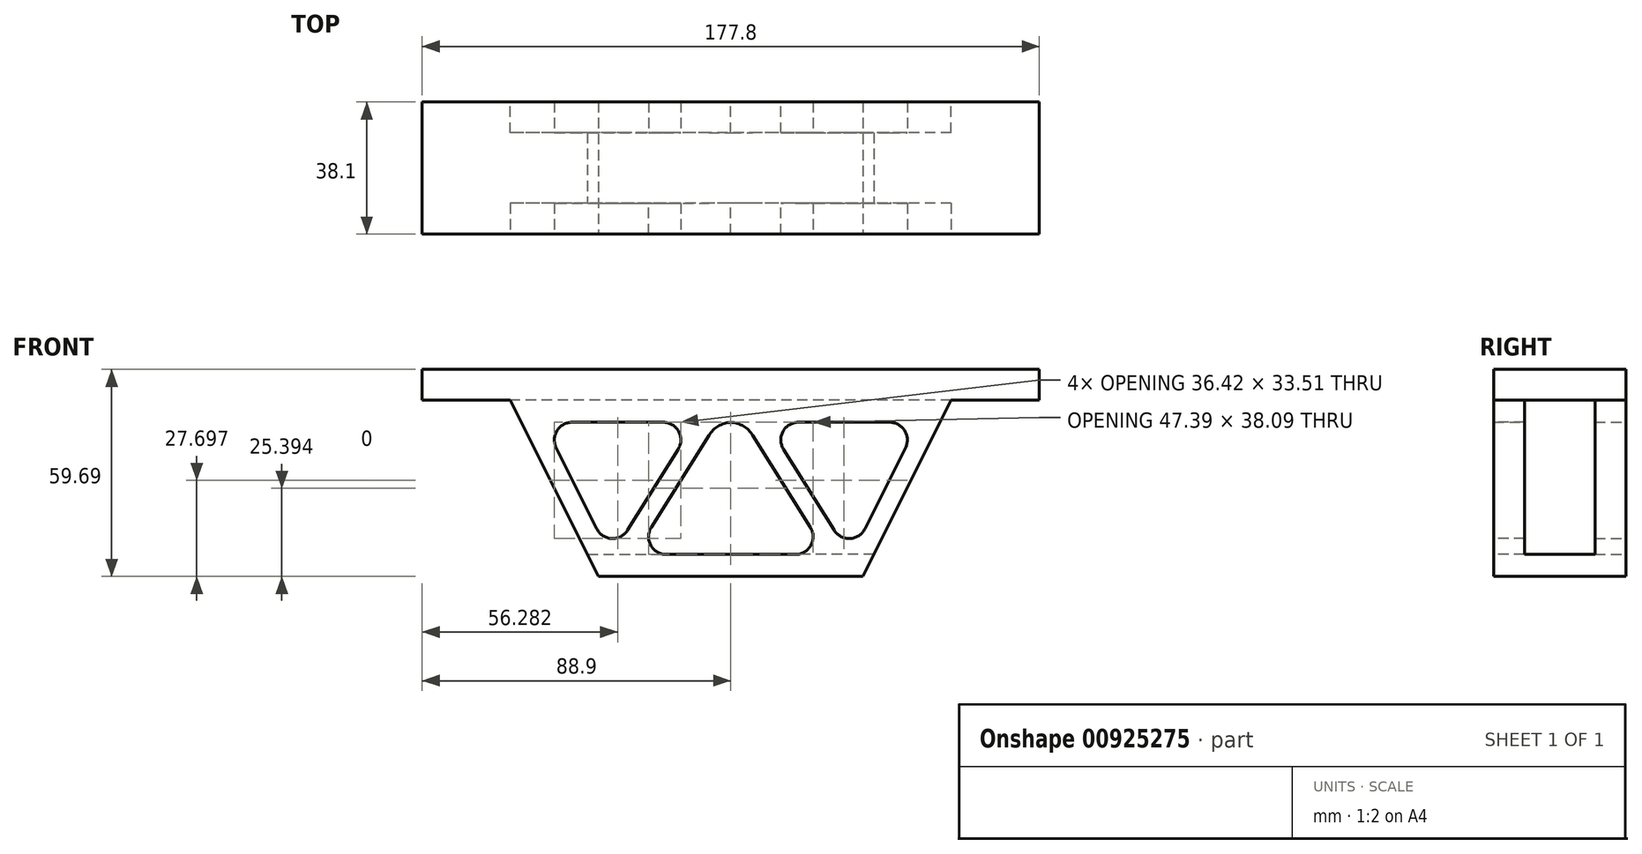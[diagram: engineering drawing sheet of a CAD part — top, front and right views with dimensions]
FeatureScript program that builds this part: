
annotation { "Feature Type Name" : "Feature", "Feature Type Description" : "" }
export const myFeature = defineFeature(function(context is Context, id is Id, definition is map)
    precondition{}
    {
        {
            var Q0;
            Q0=qCreatedBy(makeId("Right.planeOp"),FACE);
            var sketch = newSketch(context, id + "F0", { "sketchPlane" : qUnion([Q0])});
            skLineSegment(sketch, "E0.bottom", {"start": v(0, 0) * mm, "end": v(38.1, 0) * mm});
            skLineSegment(sketch, "E0.top", {"start": v(0, 8.9) * mm, "end": v(38.1, 8.9) * mm});
            skLineSegment(sketch, "E0.left", {"start": v(0, 0) * mm, "end": v(0, 8.9) * mm});
            skLineSegment(sketch, "E0.right", {"start": v(38.1, 0) * mm, "end": v(38.1, 8.9) * mm});
            skSolve(sketch);
        }
        {
            var Q0;
            Q0=makeQuery(id+"F0.imprint","IMPRINT",FACE,{"disambiguationData":[TD([[makeQuery(id+"F0.imprint","IMPRINT",EDGE,{"derivedFrom":sQuery(id+"F0.wireOp",EDGE,"E0.bottom")}),1.0]])]});
            extrude(context, id + "F1", {"entities" : qUnion([Q0]), "depth" : 177.8 * mm, "offsetDistance" : 25.4 * mm});
        }
        {
            var Q0;
            Q0=makeQuery(id+"F1.opExtrude","SWEPT_FACE",FACE,{"disambiguationData":[OSD([sQuery(id+"F0.wireOp",EDGE,"E0.left")])]});
            var sketch = newSketch(context, id + "F2", { "sketchPlane" : qUnion([Q0])});
            skLineSegment(sketch, "E1", {"start": v(0, 0) * mm, "end": v(25.4, 0) * mm});
            skLineSegment(sketch, "E2", {"start": v(177.8, 0) * mm, "end": v(152.4, 0) * mm});
            skLineSegment(sketch, "E3", {"start": v(88.9, -50.8) * mm, "end": v(50.8, -50.8) * mm});
            skLineSegment(sketch, "E4", {"start": v(88.9, -50.8) * mm, "end": v(127, -50.8) * mm});
            skLineSegment(sketch, "E5", {"start": v(152.4, 0) * mm, "end": v(127, -50.8) * mm});
            skLineSegment(sketch, "E6", {"start": v(50.8, -50.8) * mm, "end": v(25.4, 0) * mm});
            skLineSegment(sketch, "E7", {"start": v(25.4, 0) * mm, "end": v(25.4, -6.35) * mm});
            skLineSegment(sketch, "E8", {"start": v(25.4, -6.35) * mm, "end": v(152.4, -6.35) * mm});
            skLineSegment(sketch, "E9", {"start": v(25.4, 0) * mm, "end": v(31.75, 0) * mm});
            skLineSegment(sketch, "E10", {"start": v(50.8, -50.8) * mm, "end": v(57.15, -50.8) * mm});
            skLineSegment(sketch, "E11", {"start": v(152.4, 0) * mm, "end": v(146.05, 0) * mm});
            skLineSegment(sketch, "E12", {"start": v(127, -50.8) * mm, "end": v(120.65, -50.8) * mm});
            skLineSegment(sketch, "E13", {"start": v(31.75, 0) * mm, "end": v(57.15, -50.8) * mm});
            skLineSegment(sketch, "E14", {"start": v(120.65, -50.8) * mm, "end": v(146.05, 0) * mm});
            skPoint(sketch, "E15", {"position": v(88.9, 0) * mm});
            skLineSegment(sketch, "E16", {"start": v(88.9, 0) * mm, "end": v(82.55, 0) * mm});
            skLineSegment(sketch, "E17", {"start": v(88.9, 0) * mm, "end": v(95.25, 0) * mm});
            skLineSegment(sketch, "E18", {"start": v(120.65, -50.8) * mm, "end": v(88.9, 0) * mm});
            skLineSegment(sketch, "E19", {"start": v(127, -50.8) * mm, "end": v(95.25, 0) * mm});
            skLineSegment(sketch, "E20", {"start": v(50.8, -50.8) * mm, "end": v(82.55, 0) * mm});
            skLineSegment(sketch, "E21", {"start": v(57.15, -50.8) * mm, "end": v(88.9, 0) * mm});
            skLineSegment(sketch, "E22", {"start": v(130.17, -44.45) * mm, "end": v(47.62, -44.45) * mm});
            skLineSegment(sketch, "E23", {"start": v(31.75, 0) * mm, "end": v(146.05, 0) * mm});
            skSolve(sketch);
        }
        {
            var Q0;
            {var subQ0=sQuery(id+"F2.wireOp",EDGE,"E13");var subQ1=sQuery(id+"F2.wireOp",EDGE,"E8");var subQ2=makeQuery(id+"F2.imprint","INTERSECT",VERTEX,{"derivedFrom":[subQ1,subQ0]});Q0=makeQuery(id+"F2.imprint","IMPRINT",FACE,{"disambiguationData":[TD([[makeQuery(id+"F2.imprint","IMPRINT",EDGE,{"disambiguationData":[TD([[subQ2,-1.0]])],"derivedFrom":subQ1}),1.0]])]});}
            var Q1;
            {var subQ5=sQuery(id+"F2.wireOp",EDGE,"E16");Q1=makeQuery(id+"F2.imprint","IMPRINT",FACE,{"disambiguationData":[TD([[makeQuery(id+"F2.imprint","IMPRINT",EDGE,{"derivedFrom":subQ5}),1.0]])]});}
            var Q2;
            {var subQ0=sQuery(id+"F2.wireOp",EDGE,"E18");var subQ1=sQuery(id+"F2.wireOp",EDGE,"E8");var subQ2=makeQuery(id+"F2.imprint","INTERSECT",VERTEX,{"derivedFrom":[subQ1,subQ0]});Q2=makeQuery(id+"F2.imprint","IMPRINT",FACE,{"disambiguationData":[TD([[makeQuery(id+"F2.imprint","IMPRINT",EDGE,{"disambiguationData":[TD([[subQ2,1.0]])],"derivedFrom":subQ1}),1.0]])]});}
            var Q3;
            {var subQ5=sQuery(id+"F2.wireOp",EDGE,"E17");Q3=makeQuery(id+"F2.imprint","IMPRINT",FACE,{"disambiguationData":[TD([[makeQuery(id+"F2.imprint","IMPRINT",EDGE,{"derivedFrom":subQ5}),1.0]])]});}
            var Q4;
            {var subQ0=sQuery(id+"F2.wireOp",EDGE,"E19");var subQ1=sQuery(id+"F2.wireOp",EDGE,"E8");var subQ2=makeQuery(id+"F2.imprint","INTERSECT",VERTEX,{"derivedFrom":[subQ1,subQ0]});Q4=makeQuery(id+"F2.imprint","IMPRINT",FACE,{"disambiguationData":[TD([[makeQuery(id+"F2.imprint","IMPRINT",EDGE,{"disambiguationData":[TD([[subQ2,-1.0]])],"derivedFrom":subQ1}),1.0]])]});}
            var Q5;
            {var subQ0=sQuery(id+"F2.wireOp",EDGE,"E11");Q5=makeQuery(id+"F2.imprint","IMPRINT",FACE,{"disambiguationData":[TD([[makeQuery(id+"F2.imprint","IMPRINT",EDGE,{"derivedFrom":subQ0}),1.0]])]});}
            var Q6;
            {var subQ0=sQuery(id+"F2.wireOp",EDGE,"E8");var subQ1=sQuery(id+"F2.wireOp",EDGE,"E5");var subQ2=makeQuery(id+"F2.imprint","INTERSECT",VERTEX,{"derivedFrom":[subQ1,subQ0]});Q6=makeQuery(id+"F2.imprint","IMPRINT",FACE,{"disambiguationData":[TD([[makeQuery(id+"F2.imprint","IMPRINT",EDGE,{"disambiguationData":[TD([[subQ2,-1.0]])],"derivedFrom":subQ1}),-1.0]])]});}
            var Q7;
            {var subQ3=sQuery(id+"F2.wireOp",EDGE,"E22");var subQ5=sQuery(id+"F2.wireOp",EDGE,"E14");var subQ6=makeQuery(id+"F2.imprint","INTERSECT",VERTEX,{"derivedFrom":[subQ5,subQ3]});Q7=makeQuery(id+"F2.imprint","IMPRINT",FACE,{"disambiguationData":[TD([[makeQuery(id+"F2.imprint","IMPRINT",EDGE,{"disambiguationData":[TD([[subQ6,1.0]])],"derivedFrom":subQ5}),-1.0]])]});}
            var Q8;
            {var subQ0=sQuery(id+"F2.wireOp",EDGE,"E19");var subQ3=sQuery(id+"F2.wireOp",EDGE,"E14");var subQ5=makeQuery(id+"F2.imprint","INTERSECT",VERTEX,{"derivedFrom":[subQ3,subQ0]});Q8=makeQuery(id+"F2.imprint","IMPRINT",FACE,{"disambiguationData":[TD([[makeQuery(id+"F2.imprint","IMPRINT",EDGE,{"disambiguationData":[TD([[subQ5,1.0]])],"derivedFrom":subQ3}),-1.0]])]});}
            var Q9;
            {var subQ3=sQuery(id+"F2.wireOp",EDGE,"E19");var subQ5=sQuery(id+"F2.wireOp",EDGE,"E22");var subQ7=makeQuery(id+"F2.imprint","INTERSECT",VERTEX,{"derivedFrom":[subQ3,subQ5]});Q9=makeQuery(id+"F2.imprint","IMPRINT",FACE,{"disambiguationData":[TD([[makeQuery(id+"F2.imprint","IMPRINT",EDGE,{"disambiguationData":[TD([[subQ7,1.0]])],"derivedFrom":subQ3}),1.0]])]});}
            var Q10;
            {var subQ0=sQuery(id+"F2.wireOp",EDGE,"E19");var subQ1=sQuery(id+"F2.wireOp",EDGE,"E8");var subQ2=makeQuery(id+"F2.imprint","INTERSECT",VERTEX,{"derivedFrom":[subQ1,subQ0]});Q10=makeQuery(id+"F2.imprint","IMPRINT",FACE,{"disambiguationData":[TD([[makeQuery(id+"F2.imprint","IMPRINT",EDGE,{"disambiguationData":[TD([[subQ2,1.0]])],"derivedFrom":subQ1}),-1.0]])]});}
            var Q11;
            {var subQ0=sQuery(id+"F2.wireOp",EDGE,"E22");var subQ5=sQuery(id+"F2.wireOp",EDGE,"E18");var subQ6=makeQuery(id+"F2.imprint","INTERSECT",VERTEX,{"derivedFrom":[subQ5,subQ0]});Q11=makeQuery(id+"F2.imprint","IMPRINT",FACE,{"disambiguationData":[TD([[makeQuery(id+"F2.imprint","IMPRINT",EDGE,{"disambiguationData":[TD([[subQ6,-1.0]])],"derivedFrom":subQ0}),1.0]])]});}
            var Q12;
            {var subQ0=sQuery(id+"F2.wireOp",EDGE,"E20");var subQ1=sQuery(id+"F2.wireOp",EDGE,"E8");var subQ2=makeQuery(id+"F2.imprint","INTERSECT",VERTEX,{"derivedFrom":[subQ1,subQ0]});Q12=makeQuery(id+"F2.imprint","IMPRINT",FACE,{"disambiguationData":[TD([[makeQuery(id+"F2.imprint","IMPRINT",EDGE,{"disambiguationData":[TD([[subQ2,-1.0]])],"derivedFrom":subQ1}),-1.0]])]});}
            var Q13;
            {var subQ0=sQuery(id+"F2.wireOp",EDGE,"E20");var subQ1=sQuery(id+"F2.wireOp",EDGE,"E13");var subQ2=makeQuery(id+"F2.imprint","INTERSECT",VERTEX,{"derivedFrom":[subQ1,subQ0]});Q13=makeQuery(id+"F2.imprint","IMPRINT",FACE,{"disambiguationData":[TD([[makeQuery(id+"F2.imprint","IMPRINT",EDGE,{"disambiguationData":[TD([[subQ2,-1.0]])],"derivedFrom":subQ0}),-1.0]])]});}
            var Q14;
            {var subQ0=sQuery(id+"F2.wireOp",EDGE,"E20");var subQ3=sQuery(id+"F2.wireOp",EDGE,"E13");var subQ5=makeQuery(id+"F2.imprint","INTERSECT",VERTEX,{"derivedFrom":[subQ3,subQ0]});Q14=makeQuery(id+"F2.imprint","IMPRINT",FACE,{"disambiguationData":[TD([[makeQuery(id+"F2.imprint","IMPRINT",EDGE,{"disambiguationData":[TD([[subQ5,-1.0]])],"derivedFrom":subQ3}),-1.0]])]});}
            var Q15;
            {var subQ0=sQuery(id+"F2.wireOp",EDGE,"E22");var subQ1=sQuery(id+"F2.wireOp",EDGE,"E6");var subQ2=makeQuery(id+"F2.imprint","INTERSECT",VERTEX,{"derivedFrom":[subQ1,subQ0]});Q15=makeQuery(id+"F2.imprint","IMPRINT",FACE,{"disambiguationData":[TD([[makeQuery(id+"F2.imprint","IMPRINT",EDGE,{"disambiguationData":[TD([[subQ2,-1.0]])],"derivedFrom":subQ1}),-1.0]])]});}
            var Q16;
            {var subQ0=sQuery(id+"F2.wireOp",EDGE,"E9");Q16=makeQuery(id+"F2.imprint","IMPRINT",FACE,{"disambiguationData":[TD([[makeQuery(id+"F2.imprint","IMPRINT",EDGE,{"derivedFrom":subQ0}),1.0]])]});}
            var Q17;
            {var subQ0=sQuery(id+"F2.wireOp",EDGE,"E20");var subQ5=sQuery(id+"F2.wireOp",EDGE,"E13");var subQ6=makeQuery(id+"F2.imprint","INTERSECT",VERTEX,{"derivedFrom":[subQ5,subQ0]});Q17=makeQuery(id+"F2.imprint","IMPRINT",FACE,{"disambiguationData":[TD([[makeQuery(id+"F2.imprint","IMPRINT",EDGE,{"disambiguationData":[TD([[subQ6,1.0]])],"derivedFrom":subQ5}),-1.0]])]});}
            extrude(context, id + "F3", {"entities" : qUnion([Q0, Q1, Q2, Q3, Q4, Q5, Q6, Q7, Q8, Q9, Q10, Q11, Q12, Q13, Q14, Q15, Q16, Q17]), "operationType" : NewBodyOperationType.ADD, "oppositeDirection" : true, "depth" : 8.9 * mm, "offsetDistance" : 25.4 * mm});
        }
        {
            var Q0;
            Q0=makeQuery(id+"F1.opExtrude","SWEPT_FACE",FACE,{"disambiguationData":[OSD([sQuery(id+"F0.wireOp",EDGE,"E0.right")])]});
            var sketch = newSketch(context, id + "F4", { "sketchPlane" : qUnion([Q0])});
            skPoint(sketch, "E24", {"position": v(-146.05, 0) * mm});
            skPoint(sketch, "E25", {"position": v(-82.55, 0) * mm});
            skPoint(sketch, "E26", {"position": v(-25.4, -6.35) * mm});
            skPoint(sketch, "E27", {"position": v(-88.9, 0) * mm});
            skPoint(sketch, "E28", {"position": v(-57.15, -50.8) * mm});
            skPoint(sketch, "E29", {"position": v(-31.75, 0) * mm});
            skPoint(sketch, "E30", {"position": v(-120.65, -50.8) * mm});
            skPoint(sketch, "E31", {"position": v(-50.8, -50.8) * mm});
            skPoint(sketch, "E32", {"position": v(-152.4, 0) * mm});
            skPoint(sketch, "E33", {"position": v(-95.25, 0) * mm});
            skPoint(sketch, "E34", {"position": v(-127, -50.8) * mm});
            skPoint(sketch, "E35", {"position": v(-25.4, 0) * mm});
            skPoint(sketch, "E36", {"position": v(-47.62, -44.45) * mm});
            skLineSegment(sketch, "E37", {"start": v(-152.4, 0) * mm, "end": v(-127, -50.8) * mm});
            skLineSegment(sketch, "E38", {"start": v(-127, -50.8) * mm, "end": v(-50.8, -50.8) * mm});
            skLineSegment(sketch, "E39", {"start": v(-50.8, -50.8) * mm, "end": v(-25.4, 0) * mm});
            skLineSegment(sketch, "E40", {"start": v(-25.4, 0) * mm, "end": v(-152.4, 0) * mm});
            skLineSegment(sketch, "E41", {"start": v(-146.05, 0) * mm, "end": v(-120.65, -50.8) * mm});
            skLineSegment(sketch, "E42", {"start": v(-25.4, -6.35) * mm, "end": v(-156.41, -6.35) * mm});
            skLineSegment(sketch, "E43", {"start": v(-95.25, 0) * mm, "end": v(-127, -50.8) * mm});
            skLineSegment(sketch, "E44", {"start": v(-120.65, -50.8) * mm, "end": v(-88.9, 0) * mm});
            skLineSegment(sketch, "E45", {"start": v(-88.9, 0) * mm, "end": v(-57.15, -50.8) * mm});
            skLineSegment(sketch, "E46", {"start": v(-82.55, 0) * mm, "end": v(-50.8, -50.8) * mm});
            skLineSegment(sketch, "E47", {"start": v(-47.62, -44.45) * mm, "end": v(-150.27, -44.45) * mm});
            skLineSegment(sketch, "E48", {"start": v(-57.15, -50.8) * mm, "end": v(-31.75, 0) * mm});
            skSolve(sketch);
        }
        {
            var Q0;
            {var subQ0=sQuery(id+"F4.wireOp",EDGE,"E41");var subQ1=sQuery(id+"F4.wireOp",EDGE,"E40");var subQ2=makeQuery(id+"F4.imprint","INTERSECT",VERTEX,{"derivedFrom":[subQ1,subQ0]});Q0=makeQuery(id+"F4.imprint","IMPRINT",FACE,{"disambiguationData":[TD([[makeQuery(id+"F4.imprint","IMPRINT",EDGE,{"disambiguationData":[TD([[subQ2,-1.0]])],"derivedFrom":subQ1}),-1.0]])]});}
            var Q1;
            {var subQ0=sQuery(id+"F4.wireOp",EDGE,"E40");var subQ5=sQuery(id+"F4.wireOp",EDGE,"E41");var subQ6=makeQuery(id+"F4.imprint","INTERSECT",VERTEX,{"derivedFrom":[subQ0,subQ5]});Q1=makeQuery(id+"F4.imprint","IMPRINT",FACE,{"disambiguationData":[TD([[makeQuery(id+"F4.imprint","IMPRINT",EDGE,{"disambiguationData":[TD([[subQ6,-1.0]])],"derivedFrom":subQ5}),-1.0]])]});}
            var Q2;
            {var subQ3=sQuery(id+"F4.wireOp",EDGE,"E44");var subQ5=sQuery(id+"F4.wireOp",EDGE,"E42");var subQ7=makeQuery(id+"F4.imprint","INTERSECT",VERTEX,{"derivedFrom":[subQ5,subQ3]});Q2=makeQuery(id+"F4.imprint","IMPRINT",FACE,{"disambiguationData":[TD([[makeQuery(id+"F4.imprint","IMPRINT",EDGE,{"disambiguationData":[TD([[subQ7,-1.0]])],"derivedFrom":subQ5}),-1.0]])]});}
            var Q3;
            {var subQ0=sQuery(id+"F4.wireOp",EDGE,"E45");var subQ1=sQuery(id+"F4.wireOp",EDGE,"E42");var subQ2=makeQuery(id+"F4.imprint","INTERSECT",VERTEX,{"derivedFrom":[subQ1,subQ0]});Q3=makeQuery(id+"F4.imprint","IMPRINT",FACE,{"disambiguationData":[TD([[makeQuery(id+"F4.imprint","IMPRINT",EDGE,{"disambiguationData":[TD([[subQ2,-1.0]])],"derivedFrom":subQ1}),-1.0]])]});}
            var Q4;
            {var subQ3=sQuery(id+"F4.wireOp",EDGE,"E46");var subQ5=sQuery(id+"F4.wireOp",EDGE,"E42");var subQ6=makeQuery(id+"F4.imprint","INTERSECT",VERTEX,{"derivedFrom":[subQ5,subQ3]});Q4=makeQuery(id+"F4.imprint","IMPRINT",FACE,{"disambiguationData":[TD([[makeQuery(id+"F4.imprint","IMPRINT",EDGE,{"disambiguationData":[TD([[subQ6,-1.0]])],"derivedFrom":subQ5}),-1.0]])]});}
            var Q5;
            {var subQ0=sQuery(id+"F4.wireOp",EDGE,"E46");var subQ1=sQuery(id+"F4.wireOp",EDGE,"E40");var subQ2=makeQuery(id+"F4.imprint","INTERSECT",VERTEX,{"derivedFrom":[subQ1,subQ0]});Q5=makeQuery(id+"F4.imprint","IMPRINT",FACE,{"disambiguationData":[TD([[makeQuery(id+"F4.imprint","IMPRINT",EDGE,{"disambiguationData":[TD([[subQ2,-1.0]])],"derivedFrom":subQ1}),-1.0]])]});}
            var Q6;
            {var subQ1=sQuery(id+"F4.wireOp",EDGE,"E39");var subQ3=sQuery(id+"F4.wireOp",EDGE,"E42");var subQ4=makeQuery(id+"F4.imprint","INTERSECT",VERTEX,{"derivedFrom":[subQ1,subQ3]});Q6=makeQuery(id+"F4.imprint","IMPRINT",FACE,{"disambiguationData":[TD([[makeQuery(id+"F4.imprint","IMPRINT",EDGE,{"disambiguationData":[TD([[subQ4,-1.0]])],"derivedFrom":subQ3}),-1.0]])]});}
            var Q7;
            {var subQ0=sQuery(id+"F4.wireOp",EDGE,"E47");var subQ1=sQuery(id+"F4.wireOp",EDGE,"E39");var subQ2=makeQuery(id+"F4.imprint","INTERSECT",VERTEX,{"derivedFrom":[subQ1,subQ0]});Q7=makeQuery(id+"F4.imprint","IMPRINT",FACE,{"disambiguationData":[TD([[makeQuery(id+"F4.imprint","IMPRINT",EDGE,{"disambiguationData":[TD([[subQ2,-1.0]])],"derivedFrom":subQ1}),1.0]])]});}
            var Q8;
            {var subQ1=sQuery(id+"F4.wireOp",EDGE,"E39");var subQ3=sQuery(id+"F4.wireOp",EDGE,"E47");var subQ4=makeQuery(id+"F4.imprint","INTERSECT",VERTEX,{"derivedFrom":[subQ1,subQ3]});Q8=makeQuery(id+"F4.imprint","IMPRINT",FACE,{"disambiguationData":[TD([[makeQuery(id+"F4.imprint","IMPRINT",EDGE,{"disambiguationData":[TD([[subQ4,-1.0]])],"derivedFrom":subQ3}),1.0]])]});}
            var Q9;
            {var subQ0=sQuery(id+"F4.wireOp",EDGE,"E46");var subQ3=sQuery(id+"F4.wireOp",EDGE,"E48");var subQ5=makeQuery(id+"F4.imprint","INTERSECT",VERTEX,{"derivedFrom":[subQ0,subQ3]});Q9=makeQuery(id+"F4.imprint","IMPRINT",FACE,{"disambiguationData":[TD([[makeQuery(id+"F4.imprint","IMPRINT",EDGE,{"disambiguationData":[TD([[subQ5,-1.0]])],"derivedFrom":subQ0}),-1.0]])]});}
            var Q10;
            {var subQ3=sQuery(id+"F4.wireOp",EDGE,"E47");var subQ5=sQuery(id+"F4.wireOp",EDGE,"E46");var subQ6=makeQuery(id+"F4.imprint","INTERSECT",VERTEX,{"derivedFrom":[subQ5,subQ3]});Q10=makeQuery(id+"F4.imprint","IMPRINT",FACE,{"disambiguationData":[TD([[makeQuery(id+"F4.imprint","IMPRINT",EDGE,{"disambiguationData":[TD([[subQ6,-1.0]])],"derivedFrom":subQ5}),-1.0]])]});}
            var Q11;
            {var subQ0=sQuery(id+"F4.wireOp",EDGE,"E46");var subQ1=sQuery(id+"F4.wireOp",EDGE,"E42");var subQ2=makeQuery(id+"F4.imprint","INTERSECT",VERTEX,{"derivedFrom":[subQ1,subQ0]});Q11=makeQuery(id+"F4.imprint","IMPRINT",FACE,{"disambiguationData":[TD([[makeQuery(id+"F4.imprint","IMPRINT",EDGE,{"disambiguationData":[TD([[subQ2,-1.0]])],"derivedFrom":subQ1}),1.0]])]});}
            var Q12;
            {var subQ0=sQuery(id+"F4.wireOp",EDGE,"E44");var subQ5=sQuery(id+"F4.wireOp",EDGE,"E47");var subQ6=makeQuery(id+"F4.imprint","INTERSECT",VERTEX,{"derivedFrom":[subQ0,subQ5]});Q12=makeQuery(id+"F4.imprint","IMPRINT",FACE,{"disambiguationData":[TD([[makeQuery(id+"F4.imprint","IMPRINT",EDGE,{"disambiguationData":[TD([[subQ6,1.0]])],"derivedFrom":subQ5}),1.0]])]});}
            var Q13;
            {var subQ0=sQuery(id+"F4.wireOp",EDGE,"E44");var subQ1=sQuery(id+"F4.wireOp",EDGE,"E42");var subQ2=makeQuery(id+"F4.imprint","INTERSECT",VERTEX,{"derivedFrom":[subQ1,subQ0]});Q13=makeQuery(id+"F4.imprint","IMPRINT",FACE,{"disambiguationData":[TD([[makeQuery(id+"F4.imprint","IMPRINT",EDGE,{"disambiguationData":[TD([[subQ2,-1.0]])],"derivedFrom":subQ1}),1.0]])]});}
            var Q14;
            {var subQ1=sQuery(id+"F4.wireOp",EDGE,"E41");var subQ3=sQuery(id+"F4.wireOp",EDGE,"E43");var subQ4=makeQuery(id+"F4.imprint","INTERSECT",VERTEX,{"derivedFrom":[subQ1,subQ3]});Q14=makeQuery(id+"F4.imprint","IMPRINT",FACE,{"disambiguationData":[TD([[makeQuery(id+"F4.imprint","IMPRINT",EDGE,{"disambiguationData":[TD([[subQ4,1.0]])],"derivedFrom":subQ3}),1.0]])]});}
            var Q15;
            {var subQ0=sQuery(id+"F4.wireOp",EDGE,"E43");var subQ3=sQuery(id+"F4.wireOp",EDGE,"E41");var subQ5=makeQuery(id+"F4.imprint","INTERSECT",VERTEX,{"derivedFrom":[subQ3,subQ0]});Q15=makeQuery(id+"F4.imprint","IMPRINT",FACE,{"disambiguationData":[TD([[makeQuery(id+"F4.imprint","IMPRINT",EDGE,{"disambiguationData":[TD([[subQ5,-1.0]])],"derivedFrom":subQ3}),-1.0]])]});}
            var Q16;
            {var subQ3=sQuery(id+"F4.wireOp",EDGE,"E47");var subQ5=sQuery(id+"F4.wireOp",EDGE,"E41");var subQ6=makeQuery(id+"F4.imprint","INTERSECT",VERTEX,{"derivedFrom":[subQ5,subQ3]});Q16=makeQuery(id+"F4.imprint","IMPRINT",FACE,{"disambiguationData":[TD([[makeQuery(id+"F4.imprint","IMPRINT",EDGE,{"disambiguationData":[TD([[subQ6,-1.0]])],"derivedFrom":subQ5}),-1.0]])]});}
            var Q17;
            {var subQ0=sQuery(id+"F4.wireOp",EDGE,"E42");var subQ1=sQuery(id+"F4.wireOp",EDGE,"E37");var subQ2=makeQuery(id+"F4.imprint","INTERSECT",VERTEX,{"derivedFrom":[subQ1,subQ0]});Q17=makeQuery(id+"F4.imprint","IMPRINT",FACE,{"disambiguationData":[TD([[makeQuery(id+"F4.imprint","IMPRINT",EDGE,{"disambiguationData":[TD([[subQ2,-1.0]])],"derivedFrom":subQ1}),1.0]])]});}
            extrude(context, id + "F5", {"entities" : qUnion([Q0, Q1, Q2, Q3, Q4, Q5, Q6, Q7, Q8, Q9, Q10, Q11, Q12, Q13, Q14, Q15, Q16, Q17]), "operationType" : NewBodyOperationType.ADD, "oppositeDirection" : true, "depth" : 8.9 * mm, "offsetDistance" : 25.4 * mm});
        }
        {
            var Q0;
            Q0=makeQuery(id+"F3.boolean.opBoolean","MERGE",FACE,{"derivedFrom":[makeQuery(id+"F1.opExtrude","SWEPT_FACE",FACE,{"disambiguationData":[OSD([sQuery(id+"F0.wireOp",EDGE,"E0.left")])]}),makeQuery(id+"F3.opExtrude","CAP_FACE",FACE,{"disambiguationData":[OSD([sQuery(id+"F2.wireOp",EDGE,"E3"),sQuery(id+"F2.wireOp",EDGE,"E4"),sQuery(id+"F2.wireOp",EDGE,"E5"),sQuery(id+"F2.wireOp",EDGE,"E6"),sQuery(id+"F2.wireOp",EDGE,"E8"),sQuery(id+"F2.wireOp",EDGE,"E9"),sQuery(id+"F2.wireOp",EDGE,"E11"),sQuery(id+"F2.wireOp",EDGE,"E13"),sQuery(id+"F2.wireOp",EDGE,"E14"),sQuery(id+"F2.wireOp",EDGE,"E16"),sQuery(id+"F2.wireOp",EDGE,"E17"),sQuery(id+"F2.wireOp",EDGE,"E18"),sQuery(id+"F2.wireOp",EDGE,"E19"),sQuery(id+"F2.wireOp",EDGE,"E20"),sQuery(id+"F2.wireOp",EDGE,"E21"),sQuery(id+"F2.wireOp",EDGE,"E22"),sQuery(id+"F2.wireOp",EDGE,"E23")])],"isStart":true})]});
            var sketch = newSketch(context, id + "F6", { "sketchPlane" : qUnion([Q0])});
            skPoint(sketch, "E49", {"position": v(152.4, 0) * mm});
            skPoint(sketch, "E50", {"position": v(127, -50.8) * mm});
            skPoint(sketch, "E51", {"position": v(50.8, -50.8) * mm});
            skPoint(sketch, "E52", {"position": v(47.62, -44.45) * mm});
            skLineSegment(sketch, "E53", {"start": v(47.62, -44.45) * mm, "end": v(50.8, -50.8) * mm});
            skLineSegment(sketch, "E54", {"start": v(50.8, -50.8) * mm, "end": v(127, -50.8) * mm});
            skLineSegment(sketch, "E55", {"start": v(127, -50.8) * mm, "end": v(130.18, -44.45) * mm});
            skLineSegment(sketch, "E56", {"start": v(130.18, -44.45) * mm, "end": v(47.62, -44.45) * mm});
            skSolve(sketch);
        }
        {
            var Q0;
            {var subQ1=sQuery(id+"F6.wireOp",EDGE,"E53");Q0=makeQuery(id+"F6.imprint","IMPRINT",FACE,{"disambiguationData":[TD([[makeQuery(id+"F6.imprint","IMPRINT",EDGE,{"derivedFrom":subQ1}),-1.0]])]});}
            extrude(context, id + "F7", {"entities" : qUnion([Q0]), "operationType" : NewBodyOperationType.ADD, "oppositeDirection" : true, "depth" : 38.1 * mm, "offsetDistance" : 25.4 * mm});
        }
        {
            var Q0;
            Q0=makeQuery(id+"F3.opExtrude","CAP_FACE",FACE,{"disambiguationData":[OSD([sQuery(id+"F2.wireOp",EDGE,"E3"),sQuery(id+"F2.wireOp",EDGE,"E4"),sQuery(id+"F2.wireOp",EDGE,"E5"),sQuery(id+"F2.wireOp",EDGE,"E6"),sQuery(id+"F2.wireOp",EDGE,"E8"),sQuery(id+"F2.wireOp",EDGE,"E9"),sQuery(id+"F2.wireOp",EDGE,"E11"),sQuery(id+"F2.wireOp",EDGE,"E13"),sQuery(id+"F2.wireOp",EDGE,"E14"),sQuery(id+"F2.wireOp",EDGE,"E16"),sQuery(id+"F2.wireOp",EDGE,"E17"),sQuery(id+"F2.wireOp",EDGE,"E18"),sQuery(id+"F2.wireOp",EDGE,"E19"),sQuery(id+"F2.wireOp",EDGE,"E20"),sQuery(id+"F2.wireOp",EDGE,"E21"),sQuery(id+"F2.wireOp",EDGE,"E22"),sQuery(id+"F2.wireOp",EDGE,"E23")])],"isStart":false});
            cPlane(context, id + "F8", {"entities" : qUnion([Q0]), "cplaneType" : CPlaneType.OFFSET, "offset" : 0 * mm, "width" : 152.4 * mm, "height" : 152.4 * mm});
        }
        {
            var Q0;
            Q0=qCreatedBy(id+"F8.planeOp",FACE);
            var sketch = newSketch(context, id + "F9", { "sketchPlane" : qUnion([Q0])});
            skPoint(sketch, "E57", {"position": v(-123.83, -44.45) * mm});
            skPoint(sketch, "E58", {"position": v(-123.47, -45.16) * mm});
            skLineSegment(sketch, "E59", {"start": v(-123.47, -45.16) * mm, "end": v(-123.83, -44.45) * mm});
            skPoint(sketch, "E60", {"position": v(-123.03, -44.45) * mm});
            skLineSegment(sketch, "E61", {"start": v(-123.47, -45.16) * mm, "end": v(-123.03, -44.45) * mm});
            skLineSegment(sketch, "E62", {"start": v(-123.03, -44.45) * mm, "end": v(-123.83, -44.45) * mm});
            skLineSegment(sketch, "E63", {"start": v(-123.83, -44.45) * mm, "end": v(-123.47, -45.16) * mm});
            skSolve(sketch);
        }
        {
            var Q0;
            Q0 = qSketchRegion(id + "F9", true);
            extrude(context, id + "F10", {"entities" : qUnion([Q0]), "operationType" : NewBodyOperationType.ADD, "depth" : 20.32 * mm, "offsetDistance" : 25.4 * mm});
        }
        {
            var Q0;
            Q0=qCreatedBy(id+"F8.planeOp",FACE);
            var sketch = newSketch(context, id + "F11", { "sketchPlane" : qUnion([Q0])});
            skPoint(sketch, "E64", {"position": v(-54.33, -45.16) * mm});
            skPoint(sketch, "E65", {"position": v(-53.98, -44.45) * mm});
            skPoint(sketch, "E66", {"position": v(-54.77, -44.45) * mm});
            skLineSegment(sketch, "E67", {"start": v(-54.33, -45.16) * mm, "end": v(-53.98, -44.45) * mm});
            skLineSegment(sketch, "E68", {"start": v(-53.98, -44.45) * mm, "end": v(-54.77, -44.45) * mm});
            skLineSegment(sketch, "E69", {"start": v(-54.77, -44.45) * mm, "end": v(-54.33, -45.16) * mm});
            skSolve(sketch);
        }
        {
            var Q0;
            Q0 = qSketchRegion(id + "F11", true);
            extrude(context, id + "F12", {"entities" : qUnion([Q0]), "operationType" : NewBodyOperationType.ADD, "depth" : 20.32 * mm, "offsetDistance" : 25.4 * mm});
        }
        {
            var Q0;
            {var subQ0=sQuery(id+"F2.wireOp",EDGE,"E20");var subQ1=sQuery(id+"F4.wireOp",EDGE,"E48");var subQ2=sQuery(id+"F2.wireOp",EDGE,"E13");var subQ3=sQuery(id+"F4.wireOp",EDGE,"E46");Q0=makeQuery(id+"F12.boolean.opBoolean","SPLIT",EDGE,{"disambiguationData":[TD([makeQuery(id+"F1.opExtrude","SWEPT_FACE",FACE,{"disambiguationData":[OSD([sQuery(id+"F0.wireOp",EDGE,"E0.left")])]})])],"derivedFrom":makeQuery(id+"F7.boolean.opBoolean","MERGE",EDGE,{"derivedFrom":[makeQuery(id+"F3.opExtrude","SWEPT_EDGE",EDGE,{"disambiguationData":[OSD([subQ2,subQ0])]}),makeQuery(id+"F5.opExtrude","SWEPT_EDGE",EDGE,{"disambiguationData":[OSD([subQ3,subQ1])]}),makeQuery(id+"F7.opExtrude","SWEPT_EDGE",EDGE,{"disambiguationData":[OSD([subQ2,subQ0])]})]})});}
            var Q1;
            {var subQ0=sQuery(id+"F2.wireOp",EDGE,"E19");var subQ1=sQuery(id+"F2.wireOp",EDGE,"E14");var subQ2=sQuery(id+"F4.wireOp",EDGE,"E41");var subQ3=sQuery(id+"F4.wireOp",EDGE,"E43");Q1=makeQuery(id+"F10.boolean.opBoolean","SPLIT",EDGE,{"disambiguationData":[TD([makeQuery(id+"F1.opExtrude","SWEPT_FACE",FACE,{"disambiguationData":[OSD([sQuery(id+"F0.wireOp",EDGE,"E0.left")])]})])],"derivedFrom":makeQuery(id+"F7.boolean.opBoolean","MERGE",EDGE,{"derivedFrom":[makeQuery(id+"F3.opExtrude","SWEPT_EDGE",EDGE,{"disambiguationData":[OSD([subQ1,subQ0])]}),makeQuery(id+"F5.opExtrude","SWEPT_EDGE",EDGE,{"disambiguationData":[OSD([subQ2,subQ3])]}),makeQuery(id+"F7.opExtrude","SWEPT_EDGE",EDGE,{"disambiguationData":[OSD([subQ1,subQ0])]})]})});}
            var Q2;
            {var subQ0=sQuery(id+"F4.wireOp",EDGE,"E43");var subQ1=sQuery(id+"F4.wireOp",EDGE,"E41");var subQ2=sQuery(id+"F2.wireOp",EDGE,"E14");var subQ3=sQuery(id+"F2.wireOp",EDGE,"E19");Q2=makeQuery(id+"F10.boolean.opBoolean","SPLIT",EDGE,{"disambiguationData":[TD([makeQuery(id+"F1.opExtrude","SWEPT_FACE",FACE,{"disambiguationData":[OSD([sQuery(id+"F0.wireOp",EDGE,"E0.right")])]})])],"derivedFrom":makeQuery(id+"F7.boolean.opBoolean","MERGE",EDGE,{"derivedFrom":[makeQuery(id+"F3.opExtrude","SWEPT_EDGE",EDGE,{"disambiguationData":[OSD([subQ2,subQ3])]}),makeQuery(id+"F5.opExtrude","SWEPT_EDGE",EDGE,{"disambiguationData":[OSD([subQ1,subQ0])]}),makeQuery(id+"F7.opExtrude","SWEPT_EDGE",EDGE,{"disambiguationData":[OSD([subQ2,subQ3])]})]})});}
            var Q3;
            Q3=makeQuery(id+"F5.opExtrude","SWEPT_EDGE",EDGE,{"disambiguationData":[OSD([sQuery(id+"F4.wireOp",EDGE,"E42"),sQuery(id+"F4.wireOp",EDGE,"E43")])]});
            var Q4;
            Q4=makeQuery(id+"F5.opExtrude","SWEPT_EDGE",EDGE,{"disambiguationData":[OSD([sQuery(id+"F4.wireOp",EDGE,"E42"),sQuery(id+"F4.wireOp",EDGE,"E48")])]});
            var Q5;
            {var subQ0=sQuery(id+"F4.wireOp",EDGE,"E48");var subQ1=sQuery(id+"F4.wireOp",EDGE,"E46");var subQ2=sQuery(id+"F2.wireOp",EDGE,"E20");var subQ3=sQuery(id+"F2.wireOp",EDGE,"E13");Q5=makeQuery(id+"F12.boolean.opBoolean","SPLIT",EDGE,{"disambiguationData":[TD([makeQuery(id+"F1.opExtrude","SWEPT_FACE",FACE,{"disambiguationData":[OSD([sQuery(id+"F0.wireOp",EDGE,"E0.right")])]})])],"derivedFrom":makeQuery(id+"F7.boolean.opBoolean","MERGE",EDGE,{"derivedFrom":[makeQuery(id+"F3.opExtrude","SWEPT_EDGE",EDGE,{"disambiguationData":[OSD([subQ3,subQ2])]}),makeQuery(id+"F5.opExtrude","SWEPT_EDGE",EDGE,{"disambiguationData":[OSD([subQ1,subQ0])]}),makeQuery(id+"F7.opExtrude","SWEPT_EDGE",EDGE,{"disambiguationData":[OSD([subQ3,subQ2])]})]})});}
            var Q6;
            Q6=makeQuery(id+"F5.opExtrude","SWEPT_EDGE",EDGE,{"disambiguationData":[OSD([sQuery(id+"F4.wireOp",EDGE,"E41"),sQuery(id+"F4.wireOp",EDGE,"E42")])]});
            var Q7;
            Q7=makeQuery(id+"F5.opExtrude","SWEPT_EDGE",EDGE,{"disambiguationData":[OSD([sQuery(id+"F4.wireOp",EDGE,"E42"),sQuery(id+"F4.wireOp",EDGE,"E46")])]});
            var Q8;
            Q8=makeQuery(id+"F3.opExtrude","SWEPT_EDGE",EDGE,{"disambiguationData":[OSD([sQuery(id+"F2.wireOp",EDGE,"E8"),sQuery(id+"F2.wireOp",EDGE,"E20")])]});
            var Q9;
            Q9=makeQuery(id+"F3.opExtrude","SWEPT_EDGE",EDGE,{"disambiguationData":[OSD([sQuery(id+"F2.wireOp",EDGE,"E8"),sQuery(id+"F2.wireOp",EDGE,"E13")])]});
            var Q10;
            Q10=makeQuery(id+"F3.opExtrude","SWEPT_EDGE",EDGE,{"disambiguationData":[OSD([sQuery(id+"F2.wireOp",EDGE,"E8"),sQuery(id+"F2.wireOp",EDGE,"E19")])]});
            var Q11;
            Q11=makeQuery(id+"F3.opExtrude","SWEPT_EDGE",EDGE,{"disambiguationData":[OSD([sQuery(id+"F2.wireOp",EDGE,"E8"),sQuery(id+"F2.wireOp",EDGE,"E14")])]});
            var Q12;
            Q12=makeQuery(id+"F3.opExtrude","SWEPT_EDGE",EDGE,{"disambiguationData":[OSD([sQuery(id+"F2.wireOp",EDGE,"E21"),sQuery(id+"F2.wireOp",EDGE,"E22")])]});
            var Q13;
            Q13=makeQuery(id+"F3.opExtrude","SWEPT_EDGE",EDGE,{"disambiguationData":[OSD([sQuery(id+"F2.wireOp",EDGE,"E18"),sQuery(id+"F2.wireOp",EDGE,"E22")])]});
            var Q14;
            Q14=makeQuery(id+"F5.opExtrude","SWEPT_EDGE",EDGE,{"disambiguationData":[OSD([sQuery(id+"F4.wireOp",EDGE,"E44"),sQuery(id+"F4.wireOp",EDGE,"E47")])]});
            var Q15;
            Q15=makeQuery(id+"F5.opExtrude","SWEPT_EDGE",EDGE,{"disambiguationData":[OSD([sQuery(id+"F4.wireOp",EDGE,"E45"),sQuery(id+"F4.wireOp",EDGE,"E47")])]});
            fillet(context, id + "F13", {"entities" : qUnion([Q0, Q1, Q2, Q3, Q4, Q5, Q6, Q7, Q8, Q9, Q10, Q11, Q12, Q13, Q14, Q15]), "radius" : 5.08 * mm, "tangentPropagation" : true, "allowEdgeOverflow" : false});
        }
        {
            var Q0;
            Q0=makeQuery(id+"F3.opExtrude","SWEPT_EDGE",EDGE,{"disambiguationData":[OSD([sQuery(id+"F2.wireOp",EDGE,"E8"),sQuery(id+"F2.wireOp",EDGE,"E21")])]});
            var Q1;
            Q1=makeQuery(id+"F3.opExtrude","SWEPT_EDGE",EDGE,{"disambiguationData":[OSD([sQuery(id+"F2.wireOp",EDGE,"E8"),sQuery(id+"F2.wireOp",EDGE,"E18")])]});
            var Q2;
            Q2=makeQuery(id+"F5.opExtrude","SWEPT_EDGE",EDGE,{"disambiguationData":[OSD([sQuery(id+"F4.wireOp",EDGE,"E42"),sQuery(id+"F4.wireOp",EDGE,"E45")])]});
            var Q3;
            Q3=makeQuery(id+"F5.opExtrude","SWEPT_EDGE",EDGE,{"disambiguationData":[OSD([sQuery(id+"F4.wireOp",EDGE,"E42"),sQuery(id+"F4.wireOp",EDGE,"E44")])]});
            fillet(context, id + "F14", {"entities" : qUnion([Q0, Q1, Q2, Q3]), "radius" : 7.95 * mm, "tangentPropagation" : true, "allowEdgeOverflow" : false});
        }
    });
